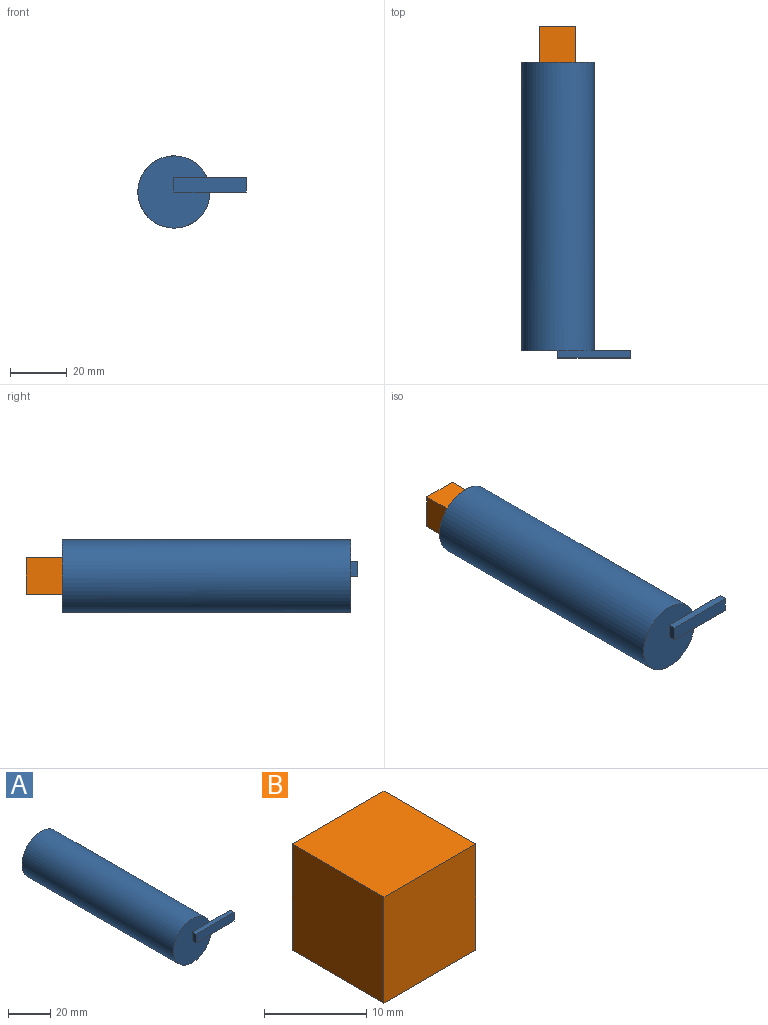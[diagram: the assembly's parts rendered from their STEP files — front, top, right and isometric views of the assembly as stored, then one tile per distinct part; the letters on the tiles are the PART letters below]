
ASSEMBLY  parts=2 mates=1
PART A: 9 faces, bbox 38.1x104.1x25.4 mm
  f0: plane 25.4x25.4mm, normal (0,-1,0), area 444mm2, adj f1,f4,f5,f6
  f1: cylinder r=12.7mm len=101.6mm, axis (0,1,0), area 8107.3mm2, adj f0,f2,f3
  f2: plane 25.4x25.4mm, normal (0,1,0), area 506.7mm2, adj f1
  f3: plane 13.76x5.08mm, normal (0,1,0), area 66.3mm2, adj f1,f4,f6,f7
  f4: plane 25.4x2.54mm, normal (0,0,1), area 64.5mm2, adj f0,f3,f5,f7,f8
  f5: plane 5.08x2.54mm, normal (-1,0,0), area 12.9mm2, adj f0,f4,f6,f8
  f6: plane 25.4x2.54mm, normal (0,0,-1), area 64.5mm2, adj f0,f3,f5,f7,f8
  f7: plane 5.08x2.54mm, normal (1,0,0), area 12.9mm2, adj f3,f4,f6,f8
  f8: plane 25.4x5.08mm, normal (0,-1,0), area 129mm2, adj f4,f5,f6,f7
PART B: 6 faces, bbox 12.7x12.7x12.7 mm
  f0: plane 12.7x12.7mm, normal (0,0,-1), area 161.3mm2, adj f1,f3,f4,f5
  f1: plane 12.7x12.7mm, normal (1,0,0), area 161.3mm2, adj f0,f2,f4,f5
  f2: plane 12.7x12.7mm, normal (0,0,1), area 161.3mm2, adj f1,f3,f4,f5
  f3: plane 12.7x12.7mm, normal (-1,0,0), area 161.3mm2, adj f0,f2,f4,f5
  f4: plane 12.7x12.7mm, normal (0,-1,0), area 161.3mm2, adj f0,f1,f2,f3
  f5: plane 12.7x12.7mm, normal (0,1,0), area 161.3mm2, adj f0,f1,f2,f3
PLACE A t=(-8.12,65.79,-19.22)mm
PLACE B rot(axis=(0,-1,0),90deg) t=(20.46,78.49,-19.22)mm
MATE slider B.f4 <-> A.f1  axis (0,-1,0) through (-8.12,65.79,-19.22)mm
